# Revit family: Hi-i-3
name_source: partatom
category: Mechanical Equipment
revit_build: Autodesk Revit 2015 (Build: 20140606_1530(x64)
units: mm (PartAtom-declared; Revit-internal decimal feet)

## types (8) — shared parameters
Depth = 0' - 8"
Keynote = Shaft options set to visibility parameters, correct shaft and size will appear when loaded into project.
Manufacturer = United Enertech Corporation
Thickness = 0' - 0 1/32"
Type Comments = Max. Size is (20" Diameter)
URL = http://unitedenertech.com

## per-type parameters (varying)
| type | Description | Exact Diameter | Model | Opening Height | Opening Width | Take-off Height |
| 6" Diameter | Round Single Blade Power/Balance Damper | 0' - 6" | i-3 | 0' - 6" | 1' - 0" | 0' - 10 1/2" |
| 8" Diameter | Round Single Blade Power/Balance Damper | 0' - 8" | i-3 | 0' - 6" | 1' - 0" | 0' - 10 1/2" |
| 10" Diameter | Round Single Blade Power/Balance Damper | 0' - 10" | i-3 | 0' - 6 3/4" | 1' - 4" | 0' - 11 1/2" |
| 12" Diameter | Round Single Blade Power/Balance Damper | 1' - 0" | i-3 | 0' - 8 1/2" | 1' - 6" | 1' - 0 1/2" |
| 14" Diameter | Round High Efficiency Power/Balance Damper | 1' - 2" | Hi-i-3 | 0' - 9 1/2" | 1' - 8" | 1' - 0 1/2" |
| 16" Diameter | Round Single Blade Power/Balance Damper | 1' - 4" | i-3 | 1' - 0" | 2' - 0" | 1' - 0 1/2" |
| 18" Diameter | Round Single Blade Power/Balance Damper | 1' - 6" | i-3 | 1' - 2" | 2' - 2" | 1' - 1 1/2" |
| 20" Diameter | Round Single Blade Power/Balance Damper | 1' - 8" | i-3 | 1' - 4" | 2' - 4" | 1' - 2 1/2" |

## geometry (parser evidence)
native form markers: Sweep x17
no freeform markers — native parametric forms only
